# Revit family: 64712203
name_source: partatom
category: Plumbing Fixtures
revit_build: Autodesk Revit 2016 (Build: 20150714_1515(x64)
units: mm (PartAtom-declared; Revit-internal decimal feet)

## family parameters
Always vertical = Yes
Cut with Voids When Loaded = No
OmniClass Number = 23.45.55.00
OmniClass Title = Sanitary Faucets, Wastes
Part Type = Normal
Room Calculation Point = No
Round Connector Dimension = Use Diameter
Shared = No
Work Plane-Based = No

## types (1)
- 64712203 Kitchen faucet
    2D/3D/BIM Files URL = http://static.hansa.com
    Aerator = Aerator
    AssetType = Fixed
    BIMObjectName = 64712203
    BodyMaterial = Brass
    Brand = Hansa
    Catalog Drawing URL = http://static.hansa.com
    Category = Kitchen
    Class = Single lever
    CloseOffRating = 0
    Color = Chrome
    Connection Size = G3/8
    ConvergoRefNr = 0087-1806-0053-FI
    Customs Code = 84818011
    Dimension Drawing URL = http://static.hansa.com
    DurationUnit = Year
    EAN Number = 4015474277410
    FDV Document URL = http://www.hansa.com
    FaucetMainMaterial = Brass
    Features = Single lever
    Finish = Polished
    Flow Drawing URL = http://static.hansa.com
    Flow Rate At 300kPa = 0.2 L/s
    FlowCoefficient = 0
    Group = Kitchen faucets
    IfcExportAs = IfcValveType
    IfcExportType = FAUCET
    InletConnectionSize = 10 mm  [stored 0.0328084 ft]
    Installation Type = Deck mounted
    Installation and Maintenance = http://static.hansa.com
    Lever Handle = Lever with H+C symbol
    ManufacterURL = http://www.hansa.com
    Manufacturer = Hansa
    ManufacturerName = Hansa
    Market = BEL;CZE;ESP;FRA;INT;ITA;NLD;SVK
    Material = Brass
    Max. Hot Water Supply = 80 °C
    Mechanical Parts = Litter filter
    Model = 64712203 Kitchen faucet
    ModelReference = 64712203
    Mounting Holes = 1 mounting hole
    NBSDescription = Water supply fittings for wash basins and troughs
    NBSReference = 45-35-70/371
    Name = 64712203 Kitchen faucet
    Name_en = 64712203 Kitchen faucet
    NominalDepth = 260 mm
    NominalHeight = 355 mm
    NominalWidth = 50 mm
    Package Weight = 1.9 kg
    Package external Dimensions = 750 x 330 x 60
    Pipes = Flexible inlet pipes
    Product Code = 64712203
    Product Datasheet = http://www.hansa.com
    Product Family = HANSALANO
    Product Image URL = http://static.hansa.com
    Product URL = http://static.hansa.com
    Projection = 205 mm
    Revision = 2
    Shape = Sculptured
    Size = 50x260x355 mm
    Spare Parts = http://static.hansa.com
    Spout Swivel Range = 120° (60° / 0°)
    Spout Type = Swivel spout
    Uniclass2 = Pr_40_30_96_45
    Uniclass2015Description = Sink manual water supply sets
    Uniclass2015Reference = Pr_40_20_87_82
    Version = 2
    VersionDate = 01/01/2019
    WarrantyDescription = http://warranty.hansa.com
    WarrantyDurationUnit = Year
    WorkingPressure = 50 - 1000 kPa

note: [stored X ft] marks values corroborated as IEEE doubles in the binary element streams (Revit-internal decimal feet)

## geometry (parser evidence)
native form markers: Sweep x5
no freeform markers — native parametric forms only
